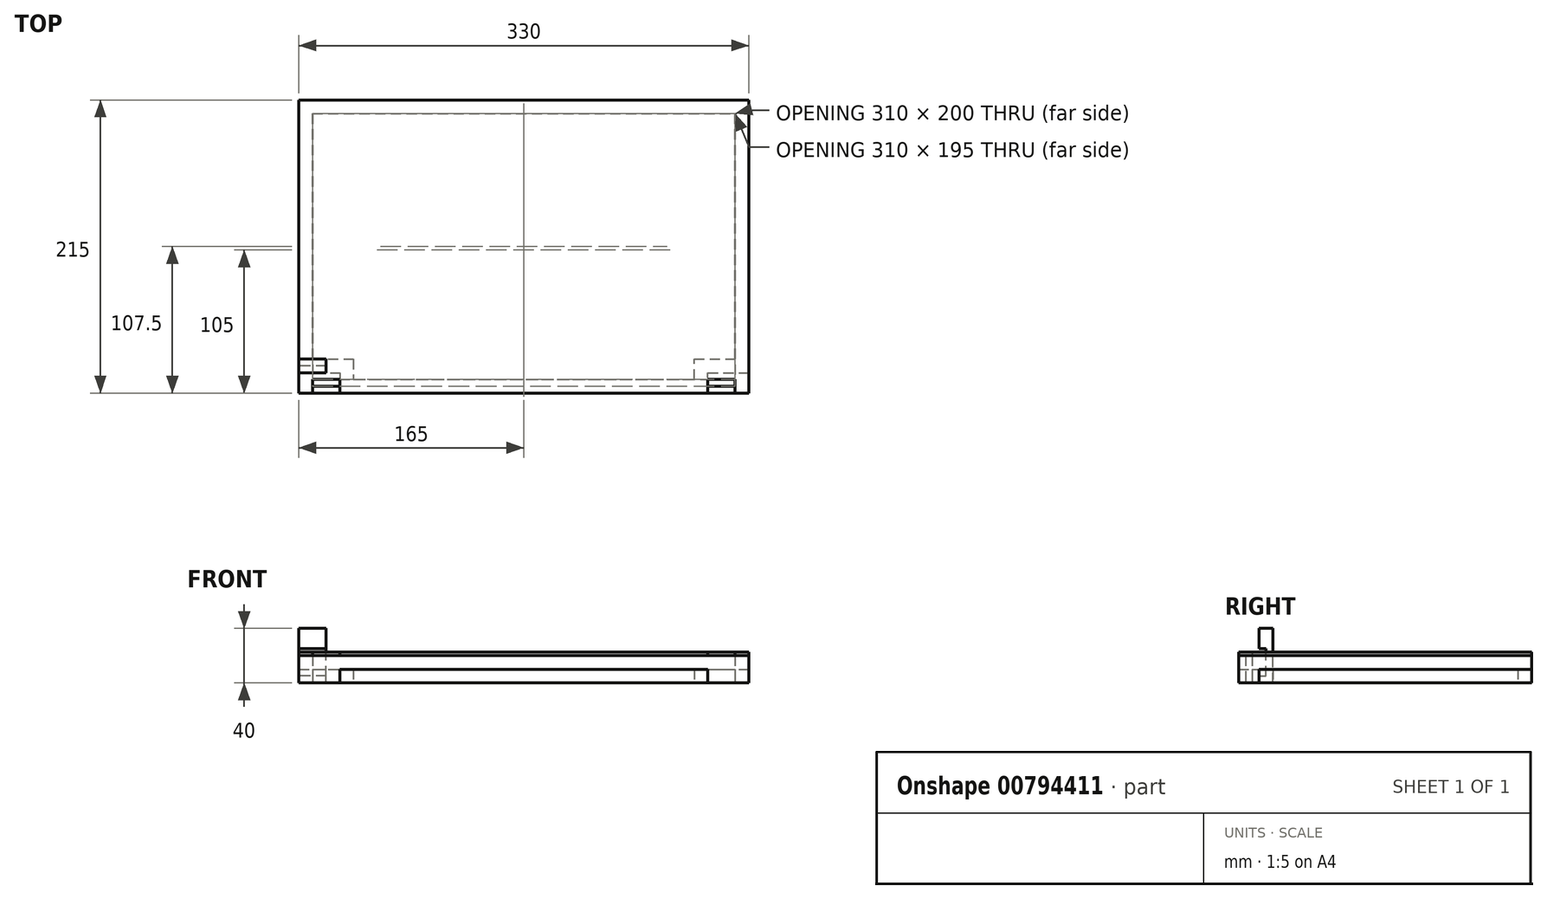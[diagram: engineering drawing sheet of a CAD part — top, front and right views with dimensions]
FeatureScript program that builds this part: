
annotation { "Feature Type Name" : "Feature", "Feature Type Description" : "" }
export const myFeature = defineFeature(function(context is Context, id is Id, definition is map)
    precondition{}
    {
        {
            var Q0;
            Q0=qCreatedBy(makeId("Top.planeOp"),FACE);
            var sketch = newSketch(context, id + "F0", { "sketchPlane" : qUnion([Q0])});
            skLineSegment(sketch, "E0.top", {"start": v(0, 200) * mm, "end": v(330, 200) * mm});
            skLineSegment(sketch, "E0.left", {"start": v(0, 0) * mm, "end": v(0, 200) * mm});
            skLineSegment(sketch, "E0.right", {"start": v(330, 0) * mm, "end": v(330, 200) * mm});
            skLineSegment(sketch, "E1", {"start": v(30, 0) * mm, "end": v(30, -15) * mm});
            skLineSegment(sketch, "E2", {"start": v(30, -15) * mm, "end": v(300, -15) * mm});
            skLineSegment(sketch, "E3", {"start": v(300, -15) * mm, "end": v(300, 0) * mm});
            skLineSegment(sketch, "E4", {"start": v(300, 0) * mm, "end": v(330, 0) * mm});
            skLineSegment(sketch, "E5.top", {"start": v(10, 190) * mm, "end": v(320, 190) * mm});
            skLineSegment(sketch, "E5.left", {"start": v(10, 10) * mm, "end": v(10, 190) * mm});
            skLineSegment(sketch, "E5.right", {"start": v(320, 10) * mm, "end": v(320, 190) * mm});
            skLineSegment(sketch, "E6", {"start": v(40, 10) * mm, "end": v(40, -5) * mm});
            skLineSegment(sketch, "E7", {"start": v(40, -5) * mm, "end": v(290, -5) * mm});
            skLineSegment(sketch, "E8", {"start": v(290, -5) * mm, "end": v(290, 10) * mm});
            skLineSegment(sketch, "E9", {"start": v(0, 0) * mm, "end": v(30, 0) * mm});
            skLineSegment(sketch, "E10", {"start": v(10, 10) * mm, "end": v(40, 10) * mm});
            skLineSegment(sketch, "E11", {"start": v(290, 10) * mm, "end": v(320, 10) * mm});
            skSolve(sketch);
        }
        {
            var Q0;
            Q0=makeQuery(id+"F0.imprint","IMPRINT",FACE,{"disambiguationData":[TD([[makeQuery(id+"F0.imprint","IMPRINT",EDGE,{"derivedFrom":sQuery(id+"F0.wireOp",EDGE,"E0.top")}),-1.0]])]});
            extrude(context, id + "F1", {"entities" : qUnion([Q0]), "depth" : 10 * mm, "offsetDistance" : 25 * mm});
        }
        {
            var Q0;
            Q0=qCreatedBy(makeId("Top.planeOp"),FACE);
            var sketch = newSketch(context, id + "F2", { "sketchPlane" : qUnion([Q0])});
            skLineSegment(sketch, "E12", {"start": v(0, 0) * mm, "end": v(0, -15) * mm, "construction": true});
            skLineSegment(sketch, "E13.bottom", {"start": v(0, -15) * mm, "end": v(330, -15) * mm});
            skLineSegment(sketch, "E13.top", {"start": v(0, 200) * mm, "end": v(330, 200) * mm});
            skLineSegment(sketch, "E13.left", {"start": v(0, -15) * mm, "end": v(0, 200) * mm});
            skLineSegment(sketch, "E13.right", {"start": v(330, -15) * mm, "end": v(330, 200) * mm});
            skLineSegment(sketch, "E14", {"start": v(0, 200) * mm, "end": v(0, 190) * mm, "construction": true});
            skLineSegment(sketch, "E15", {"start": v(0, 190) * mm, "end": v(10, 190) * mm, "construction": true});
            skLineSegment(sketch, "E16", {"start": v(330, -15) * mm, "end": v(330, -5) * mm, "construction": true});
            skLineSegment(sketch, "E17", {"start": v(330, -5) * mm, "end": v(320, -5) * mm, "construction": true});
            skLineSegment(sketch, "E18.bottom", {"start": v(10, 190) * mm, "end": v(320, 190) * mm});
            skLineSegment(sketch, "E18.left", {"start": v(10, 190) * mm, "end": v(10, -5) * mm});
            skLineSegment(sketch, "E18.right", {"start": v(320, 190) * mm, "end": v(320, -5) * mm});
            skLineSegment(sketch, "E19.bottom", {"start": v(10, -5) * mm, "end": v(30, -5) * mm, "construction": true});
            skLineSegment(sketch, "E19.top", {"start": v(10, -10) * mm, "end": v(30, -10) * mm});
            skLineSegment(sketch, "E19.left", {"start": v(10, -5) * mm, "end": v(10, -10) * mm});
            skLineSegment(sketch, "E19.right", {"start": v(30, -5) * mm, "end": v(30, -10) * mm});
            skLineSegment(sketch, "E20.bottom", {"start": v(320, -5) * mm, "end": v(300, -5) * mm, "construction": true});
            skLineSegment(sketch, "E20.top", {"start": v(320, -10) * mm, "end": v(300, -10) * mm});
            skLineSegment(sketch, "E20.left", {"start": v(320, -5) * mm, "end": v(320, -10) * mm});
            skLineSegment(sketch, "E20.right", {"start": v(300, -5) * mm, "end": v(300, -10) * mm});
            skLineSegment(sketch, "E21", {"start": v(30, -5) * mm, "end": v(300, -5) * mm});
            skSolve(sketch);
        }
        {
            var Q0;
            Q0=makeQuery(id+"F2.imprint","IMPRINT",FACE,{"disambiguationData":[TD([[makeQuery(id+"F2.imprint","IMPRINT",EDGE,{"derivedFrom":sQuery(id+"F2.wireOp",EDGE,"E13.bottom")}),1.0]])]});
            extrude(context, id + "F3", {"entities" : qUnion([Q0]), "depth" : 20 * mm, "offsetDistance" : 25 * mm});
        }
        {
            var Q0;
            Q0=qCreatedBy(makeId("Right.planeOp"),FACE);
            var sketch = newSketch(context, id + "F4", { "sketchPlane" : qUnion([Q0])});
            skLineSegment(sketch, "E22.bottom", {"start": v(0, 0) * mm, "end": v(10, 0) * mm});
            skLineSegment(sketch, "E22.top", {"start": v(0, 40) * mm, "end": v(10, 40) * mm});
            skLineSegment(sketch, "E22.right", {"start": v(10, 0) * mm, "end": v(10, 40) * mm});
            skLineSegment(sketch, "E23", {"start": v(0, 0) * mm, "end": v(0, 5) * mm});
            skLineSegment(sketch, "E24", {"start": v(0, 5) * mm, "end": v(5, 5) * mm});
            skLineSegment(sketch, "E25", {"start": v(5, 5) * mm, "end": v(5, 25) * mm});
            skLineSegment(sketch, "E26", {"start": v(5, 25) * mm, "end": v(0, 25) * mm});
            skLineSegment(sketch, "E27", {"start": v(0, 25) * mm, "end": v(0, 40) * mm});
            skSolve(sketch);
        }
        {
            var Q0;
            Q0 = qSketchRegion(id + "F4", true);
            extrude(context, id + "F5", {"entities" : qUnion([Q0]), "depth" : 20 * mm, "offsetDistance" : 25 * mm});
        }
        {
            var Q0;
            Q0=makeQuery(id+"F3.opExtrude","CAP_FACE",FACE,{"disambiguationData":[OSD([sQuery(id+"F2.wireOp",EDGE,"E13.bottom"),sQuery(id+"F2.wireOp",EDGE,"E13.top"),sQuery(id+"F2.wireOp",EDGE,"E13.left"),sQuery(id+"F2.wireOp",EDGE,"E13.right"),sQuery(id+"F2.wireOp",EDGE,"E18.bottom"),sQuery(id+"F2.wireOp",EDGE,"E18.left"),sQuery(id+"F2.wireOp",EDGE,"E18.right"),sQuery(id+"F2.wireOp",EDGE,"E19.top"),sQuery(id+"F2.wireOp",EDGE,"E19.left"),sQuery(id+"F2.wireOp",EDGE,"E19.right"),sQuery(id+"F2.wireOp",EDGE,"E20.top"),sQuery(id+"F2.wireOp",EDGE,"E20.left"),sQuery(id+"F2.wireOp",EDGE,"E20.right"),sQuery(id+"F2.wireOp",EDGE,"E21")])],"isStart":false});
            var sketch = newSketch(context, id + "F6", { "sketchPlane" : qUnion([Q0])});
            skLineSegment(sketch, "E28.bottom", {"start": v(0, 200) * mm, "end": v(330, 200) * mm});
            skLineSegment(sketch, "E28.left", {"start": v(0, 200) * mm, "end": v(0, -15) * mm});
            skLineSegment(sketch, "E28.right", {"start": v(330, 200) * mm, "end": v(330, -15) * mm});
            skLineSegment(sketch, "E29", {"start": v(330, -15) * mm, "end": v(320, -15) * mm});
            skLineSegment(sketch, "E30", {"start": v(320, -15) * mm, "end": v(320, -5) * mm});
            skLineSegment(sketch, "E31", {"start": v(320, -5) * mm, "end": v(300, -5) * mm});
            skLineSegment(sketch, "E32", {"start": v(300, -5) * mm, "end": v(300, -15) * mm});
            skLineSegment(sketch, "E33", {"start": v(300, -15) * mm, "end": v(30, -15) * mm});
            skLineSegment(sketch, "E34", {"start": v(30, -15) * mm, "end": v(30, -5) * mm});
            skLineSegment(sketch, "E35", {"start": v(30, -5) * mm, "end": v(10, -5) * mm});
            skLineSegment(sketch, "E36", {"start": v(10, -5) * mm, "end": v(10, -15) * mm});
            skLineSegment(sketch, "E37", {"start": v(10, -15) * mm, "end": v(0, -15) * mm});
            skSolve(sketch);
        }
        {
            var Q0;
            Q0 = qSketchRegion(id + "F6", true);
            extrude(context, id + "F7", {"entities" : qUnion([Q0]), "depth" : 2.5 * mm, "offsetDistance" : 25 * mm});
        }
    });
